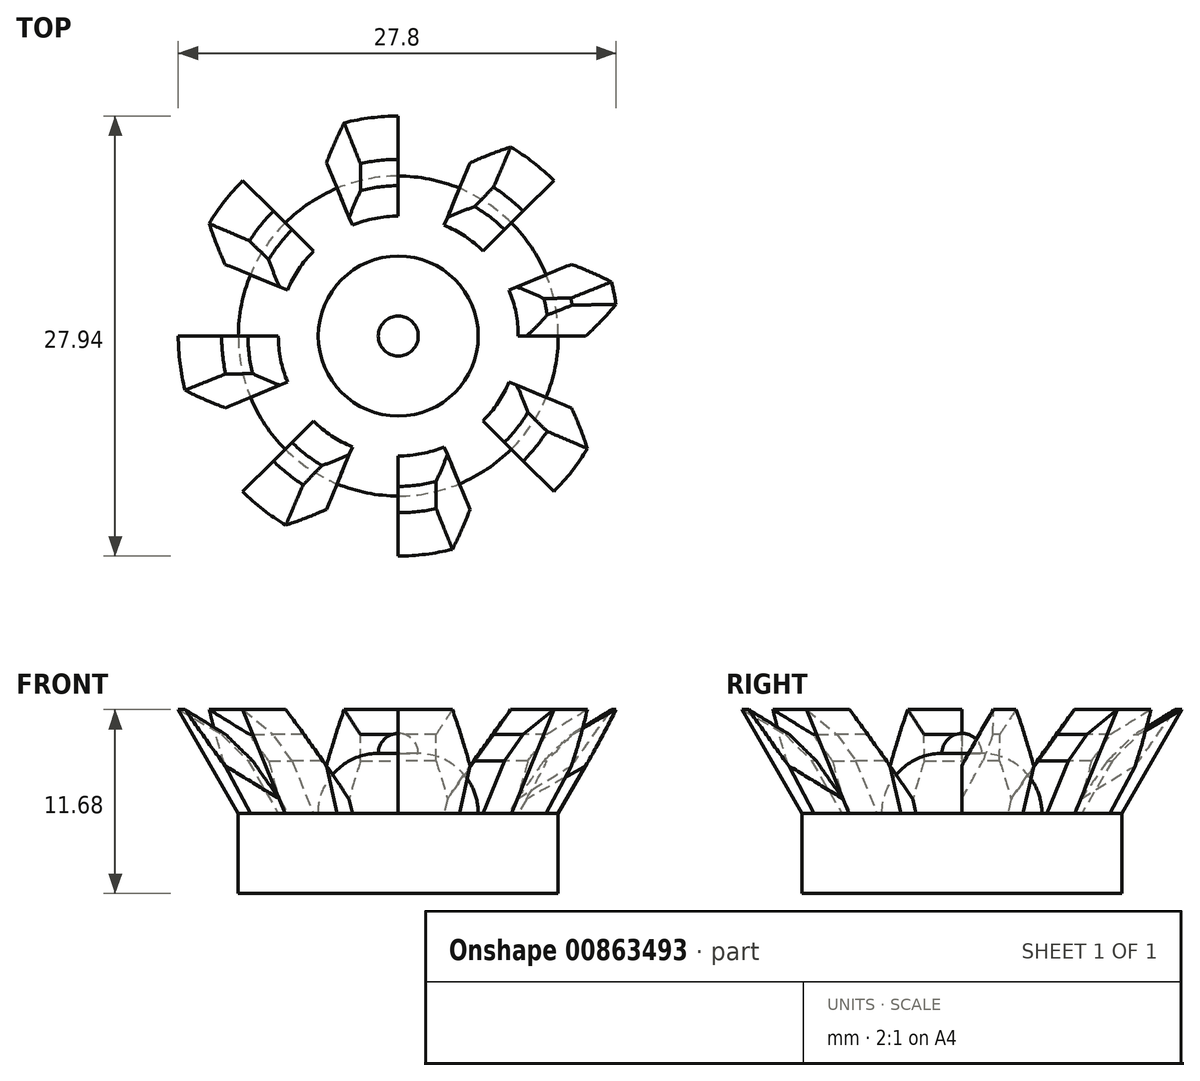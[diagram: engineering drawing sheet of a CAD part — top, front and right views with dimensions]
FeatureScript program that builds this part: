
annotation { "Feature Type Name" : "Feature", "Feature Type Description" : "" }
export const myFeature = defineFeature(function(context is Context, id is Id, definition is map)
    precondition{}
    {
        {
            var Q0;
            Q0=qCreatedBy(makeId("Top.planeOp"),FACE);
            var sketch = newSketch(context, id + "F0", { "sketchPlane" : qUnion([Q0])});
            skCircle(sketch, "E0", {"center": v(0, 0) * mm, "radius": 10.16 * mm});
            skSolve(sketch);
        }
        {
            var Q0;
            Q0=makeQuery(id+"F0.imprint","IMPRINT",FACE,{"disambiguationData":[TD([[makeQuery(id+"F0.imprint","IMPRINT",EDGE,{"derivedFrom":sQuery(id+"F0.wireOp",EDGE,"E0")}),1.0]])]});
            extrude(context, id + "F1", {"entities" : qUnion([Q0]), "depth" : 5.08 * mm, "offsetDistance" : 25.4 * mm});
        }
        {
            var Q0;
            Q0=qCreatedBy(makeId("Front.planeOp"),FACE);
            var sketch = newSketch(context, id + "F2", { "sketchPlane" : qUnion([Q0])});
            skLineSegment(sketch, "E1", {"start": v(0, 0) * mm, "end": v(0, 5.08) * mm, "construction": true});
            skLineSegment(sketch, "E2", {"start": v(0, 5.08) * mm, "end": v(7.62, 5.08) * mm, "construction": true});
            skLineSegment(sketch, "E3", {"start": v(7.62, 5.08) * mm, "end": v(10.16, 5.08) * mm});
            skLineSegment(sketch, "E4", {"start": v(10.16, 5.08) * mm, "end": v(13.97, 11.68) * mm});
            skLineSegment(sketch, "E5", {"start": v(13.97, 11.68) * mm, "end": v(10.16, 9.48) * mm});
            skLineSegment(sketch, "E6", {"start": v(10.16, 9.48) * mm, "end": v(7.62, 5.08) * mm});
            skLineSegment(sketch, "E7.MirrorCS", {"start": v(-10.16, 9.48) * mm, "end": v(-7.62, 5.08) * mm});
            skLineSegment(sketch, "E8.MirrorCS", {"start": v(-13.97, 11.68) * mm, "end": v(-10.16, 9.48) * mm});
            skLineSegment(sketch, "E9.MirrorCS", {"start": v(-10.16, 5.08) * mm, "end": v(-13.97, 11.68) * mm});
            skLineSegment(sketch, "E10.MirrorCS", {"start": v(-7.62, 5.08) * mm, "end": v(-10.16, 5.08) * mm});
            skSolve(sketch);
        }
        {
            var Q0;
            Q0=makeQuery(id+"F2.imprint","IMPRINT",FACE,{"disambiguationData":[TD([[makeQuery(id+"F2.imprint","IMPRINT",EDGE,{"derivedFrom":sQuery(id+"F2.wireOp",EDGE,"E7.MirrorCS")}),-1.0]])]});
            var Q1;
            Q1=makeQuery(id+"F2.imprint","IMPRINT",FACE,{"disambiguationData":[TD([[makeQuery(id+"F2.imprint","IMPRINT",EDGE,{"derivedFrom":sQuery(id+"F2.wireOp",EDGE,"E3")}),1.0]])]});
            var Q2;
            Q2=sQuery(id+"F2.wireOp",EDGE,"E1");
            revolve(context, id + "F3", {"operationType" : NewBodyOperationType.ADD, "surfaceOperationType" : NewSurfaceOperationType.NEW, "entities" : qUnion([Q0, Q1]), "axis" : qUnion([Q2]), "revolveType" : RevolveType.ONE_DIRECTION, "angle" : 157.5 * degree});
        }
        {
            var Q0;
            Q0=makeQuery(id+"F2.imprint","IMPRINT",FACE,{"disambiguationData":[TD([[makeQuery(id+"F2.imprint","IMPRINT",EDGE,{"derivedFrom":sQuery(id+"F2.wireOp",EDGE,"E7.MirrorCS")}),-1.0]])]});
            var Q1;
            Q1=makeQuery(id+"F2.imprint","IMPRINT",FACE,{"disambiguationData":[TD([[makeQuery(id+"F2.imprint","IMPRINT",EDGE,{"derivedFrom":sQuery(id+"F2.wireOp",EDGE,"E3")}),1.0]])]});
            var Q2;
            Q2=sQuery(id+"F2.wireOp",EDGE,"E1");
            revolve(context, id + "F4", {"operationType" : NewBodyOperationType.REMOVE, "surfaceOperationType" : NewSurfaceOperationType.NEW, "entities" : qUnion([Q0, Q1]), "axis" : qUnion([Q2]), "revolveType" : RevolveType.ONE_DIRECTION, "angle" : 135 * degree});
        }
        {
            var Q0;
            Q0=makeQuery(id+"F2.imprint","IMPRINT",FACE,{"disambiguationData":[TD([[makeQuery(id+"F2.imprint","IMPRINT",EDGE,{"derivedFrom":sQuery(id+"F2.wireOp",EDGE,"E7.MirrorCS")}),-1.0]])]});
            var Q1;
            Q1=makeQuery(id+"F2.imprint","IMPRINT",FACE,{"disambiguationData":[TD([[makeQuery(id+"F2.imprint","IMPRINT",EDGE,{"derivedFrom":sQuery(id+"F2.wireOp",EDGE,"E3")}),1.0]])]});
            var Q2;
            Q2=sQuery(id+"F2.wireOp",EDGE,"E1");
            revolve(context, id + "F5", {"operationType" : NewBodyOperationType.ADD, "surfaceOperationType" : NewSurfaceOperationType.NEW, "entities" : qUnion([Q0, Q1]), "axis" : qUnion([Q2]), "revolveType" : RevolveType.ONE_DIRECTION, "angle" : 112.5 * degree});
        }
        {
            var Q0;
            Q0=makeQuery(id+"F2.imprint","IMPRINT",FACE,{"disambiguationData":[TD([[makeQuery(id+"F2.imprint","IMPRINT",EDGE,{"derivedFrom":sQuery(id+"F2.wireOp",EDGE,"E3")}),1.0]])]});
            var Q1;
            Q1=makeQuery(id+"F2.imprint","IMPRINT",FACE,{"disambiguationData":[TD([[makeQuery(id+"F2.imprint","IMPRINT",EDGE,{"derivedFrom":sQuery(id+"F2.wireOp",EDGE,"E7.MirrorCS")}),-1.0]])]});
            var Q2;
            Q2=sQuery(id+"F2.wireOp",EDGE,"E1");
            revolve(context, id + "F6", {"operationType" : NewBodyOperationType.REMOVE, "surfaceOperationType" : NewSurfaceOperationType.NEW, "entities" : qUnion([Q0, Q1]), "axis" : qUnion([Q2]), "revolveType" : RevolveType.ONE_DIRECTION, "angle" : 90 * degree});
        }
        {
            var Q0;
            Q0=makeQuery(id+"F2.imprint","IMPRINT",FACE,{"disambiguationData":[TD([[makeQuery(id+"F2.imprint","IMPRINT",EDGE,{"derivedFrom":sQuery(id+"F2.wireOp",EDGE,"E3")}),1.0]])]});
            var Q1;
            Q1=makeQuery(id+"F2.imprint","IMPRINT",FACE,{"disambiguationData":[TD([[makeQuery(id+"F2.imprint","IMPRINT",EDGE,{"derivedFrom":sQuery(id+"F2.wireOp",EDGE,"E7.MirrorCS")}),-1.0]])]});
            var Q2;
            Q2=sQuery(id+"F2.wireOp",EDGE,"E1");
            revolve(context, id + "F7", {"operationType" : NewBodyOperationType.ADD, "surfaceOperationType" : NewSurfaceOperationType.NEW, "entities" : qUnion([Q0, Q1]), "axis" : qUnion([Q2]), "revolveType" : RevolveType.ONE_DIRECTION, "angle" : 67.5 * degree});
        }
        {
            var Q0;
            Q0=makeQuery(id+"F2.imprint","IMPRINT",FACE,{"disambiguationData":[TD([[makeQuery(id+"F2.imprint","IMPRINT",EDGE,{"derivedFrom":sQuery(id+"F2.wireOp",EDGE,"E3")}),1.0]])]});
            var Q1;
            Q1=makeQuery(id+"F2.imprint","IMPRINT",FACE,{"disambiguationData":[TD([[makeQuery(id+"F2.imprint","IMPRINT",EDGE,{"derivedFrom":sQuery(id+"F2.wireOp",EDGE,"E7.MirrorCS")}),-1.0]])]});
            var Q2;
            Q2=sQuery(id+"F2.wireOp",EDGE,"E1");
            revolve(context, id + "F8", {"operationType" : NewBodyOperationType.REMOVE, "surfaceOperationType" : NewSurfaceOperationType.NEW, "entities" : qUnion([Q0, Q1]), "axis" : qUnion([Q2]), "revolveType" : RevolveType.ONE_DIRECTION, "angle" : 45 * degree});
        }
        {
            var Q0;
            Q0=makeQuery(id+"F2.imprint","IMPRINT",FACE,{"disambiguationData":[TD([[makeQuery(id+"F2.imprint","IMPRINT",EDGE,{"derivedFrom":sQuery(id+"F2.wireOp",EDGE,"E7.MirrorCS")}),-1.0]])]});
            var Q1;
            Q1=makeQuery(id+"F2.imprint","IMPRINT",FACE,{"disambiguationData":[TD([[makeQuery(id+"F2.imprint","IMPRINT",EDGE,{"derivedFrom":sQuery(id+"F2.wireOp",EDGE,"E3")}),1.0]])]});
            var Q2;
            Q2=sQuery(id+"F2.wireOp",EDGE,"E1");
            revolve(context, id + "F9", {"operationType" : NewBodyOperationType.ADD, "surfaceOperationType" : NewSurfaceOperationType.NEW, "entities" : qUnion([Q0, Q1]), "axis" : qUnion([Q2]), "revolveType" : RevolveType.ONE_DIRECTION, "angle" : 22.5 * degree});
        }
        {
            var Q0;
            Q0=makeQuery(id+"F3.opRevolve","CAP_EDGE",EDGE,{"disambiguationData":[OSD([sQuery(id+"F2.wireOp",EDGE,"E5")])],"isStart":false});
            var Q1;
            Q1=makeQuery(id+"F4.boolean.opBoolean","COPY",EDGE,{"derivedFrom":makeQuery(id+"F4.opRevolve","CAP_EDGE",EDGE,{"disambiguationData":[OSD([sQuery(id+"F2.wireOp",EDGE,"E5")])],"isStart":false})});
            var Q2;
            Q2=makeQuery(id+"F5.opRevolve","CAP_EDGE",EDGE,{"disambiguationData":[OSD([sQuery(id+"F2.wireOp",EDGE,"E5")])],"isStart":false});
            var Q3;
            Q3=makeQuery(id+"F6.boolean.opBoolean","COPY",EDGE,{"derivedFrom":makeQuery(id+"F6.opRevolve","CAP_EDGE",EDGE,{"disambiguationData":[OSD([sQuery(id+"F2.wireOp",EDGE,"E5")]),OD(0.0)],"isStart":false})});
            var Q4;
            Q4=makeQuery(id+"F7.opRevolve","CAP_EDGE",EDGE,{"disambiguationData":[OSD([sQuery(id+"F2.wireOp",EDGE,"E5")]),OD(0.0)],"isStart":false});
            var Q5;
            Q5=makeQuery(id+"F8.boolean.opBoolean","COPY",EDGE,{"derivedFrom":makeQuery(id+"F8.opRevolve","CAP_EDGE",EDGE,{"disambiguationData":[OSD([sQuery(id+"F2.wireOp",EDGE,"E5")]),OD(1.0)],"isStart":false})});
            var Q6;
            Q6=makeQuery(id+"F9.opRevolve","CAP_EDGE",EDGE,{"disambiguationData":[OSD([sQuery(id+"F2.wireOp",EDGE,"E5")])],"isStart":false});
            var Q7;
            Q7=makeQuery(id+"F9.opRevolve","CAP_EDGE",EDGE,{"disambiguationData":[OSD([sQuery(id+"F2.wireOp",EDGE,"E5")])],"isStart":true});
            var Q8;
            Q8=makeQuery(id+"F3.opRevolve","CAP_EDGE",EDGE,{"disambiguationData":[OSD([sQuery(id+"F2.wireOp",EDGE,"E8.MirrorCS")]),OD(1.0)],"isStart":false});
            var Q9;
            Q9=makeQuery(id+"F4.boolean.opBoolean","COPY",EDGE,{"derivedFrom":makeQuery(id+"F4.opRevolve","CAP_EDGE",EDGE,{"disambiguationData":[OSD([sQuery(id+"F2.wireOp",EDGE,"E8.MirrorCS")]),OD(1.0)],"isStart":false})});
            var Q10;
            Q10=makeQuery(id+"F5.opRevolve","CAP_EDGE",EDGE,{"disambiguationData":[OSD([sQuery(id+"F2.wireOp",EDGE,"E8.MirrorCS")]),OD(1.0)],"isStart":false});
            var Q11;
            Q11=makeQuery(id+"F6.boolean.opBoolean","COPY",EDGE,{"derivedFrom":makeQuery(id+"F6.opRevolve","CAP_EDGE",EDGE,{"disambiguationData":[OSD([sQuery(id+"F2.wireOp",EDGE,"E8.MirrorCS")])],"isStart":false})});
            var Q12;
            Q12=makeQuery(id+"F7.opRevolve","CAP_EDGE",EDGE,{"disambiguationData":[OSD([sQuery(id+"F2.wireOp",EDGE,"E8.MirrorCS")])],"isStart":false});
            var Q13;
            Q13=makeQuery(id+"F8.boolean.opBoolean","COPY",EDGE,{"derivedFrom":makeQuery(id+"F8.opRevolve","CAP_EDGE",EDGE,{"disambiguationData":[OSD([sQuery(id+"F2.wireOp",EDGE,"E8.MirrorCS")])],"isStart":false})});
            var Q14;
            Q14=makeQuery(id+"F9.opRevolve","CAP_EDGE",EDGE,{"disambiguationData":[OSD([sQuery(id+"F2.wireOp",EDGE,"E8.MirrorCS")]),OD(0.0)],"isStart":false});
            var Q15;
            Q15=makeQuery(id+"F9.opRevolve","CAP_EDGE",EDGE,{"disambiguationData":[OSD([sQuery(id+"F2.wireOp",EDGE,"E8.MirrorCS")]),OD(1.0)],"isStart":false});
            chamfer(context, id + "F10", {"entities" : qUnion([Q0, Q1, Q2, Q3, Q4, Q5, Q6, Q7, Q8, Q9, Q10, Q11, Q12, Q13, Q14, Q15]), "width" : 2.16 * mm, "tangentPropagation" : true});
        }
        {
            var Q0;
            Q0=makeQuery(id+"F3.opRevolve","SWEPT_EDGE",EDGE,{"disambiguationData":[OSD([sQuery(id+"F2.wireOp",EDGE,"E5"),sQuery(id+"F2.wireOp",EDGE,"E6")])]});
            var Q1;
            Q1=makeQuery(id+"F5.opRevolve","SWEPT_EDGE",EDGE,{"disambiguationData":[OSD([sQuery(id+"F2.wireOp",EDGE,"E5"),sQuery(id+"F2.wireOp",EDGE,"E6")])]});
            var Q2;
            Q2=makeQuery(id+"F7.opRevolve","SWEPT_EDGE",EDGE,{"disambiguationData":[OSD([sQuery(id+"F2.wireOp",EDGE,"E5"),sQuery(id+"F2.wireOp",EDGE,"E6")])]});
            var Q3;
            Q3=makeQuery(id+"F9.opRevolve","SWEPT_EDGE",EDGE,{"disambiguationData":[OSD([sQuery(id+"F2.wireOp",EDGE,"E5"),sQuery(id+"F2.wireOp",EDGE,"E6")])]});
            var Q4;
            Q4=makeQuery(id+"F3.opRevolve","SWEPT_EDGE",EDGE,{"disambiguationData":[OSD([sQuery(id+"F2.wireOp",EDGE,"E7.MirrorCS"),sQuery(id+"F2.wireOp",EDGE,"E8.MirrorCS")])]});
            var Q5;
            Q5=makeQuery(id+"F5.opRevolve","SWEPT_EDGE",EDGE,{"disambiguationData":[OSD([sQuery(id+"F2.wireOp",EDGE,"E7.MirrorCS"),sQuery(id+"F2.wireOp",EDGE,"E8.MirrorCS")])]});
            var Q6;
            Q6=makeQuery(id+"F7.opRevolve","SWEPT_EDGE",EDGE,{"disambiguationData":[OSD([sQuery(id+"F2.wireOp",EDGE,"E7.MirrorCS"),sQuery(id+"F2.wireOp",EDGE,"E8.MirrorCS")])]});
            var Q7;
            Q7=makeQuery(id+"F9.opRevolve","SWEPT_EDGE",EDGE,{"disambiguationData":[OSD([sQuery(id+"F2.wireOp",EDGE,"E7.MirrorCS"),sQuery(id+"F2.wireOp",EDGE,"E8.MirrorCS")])]});
            chamfer(context, id + "F11", {"entities" : qUnion([Q0, Q1, Q2, Q3, Q4, Q5, Q6, Q7]), "width" : 4.57 * mm, "tangentPropagation" : true});
        }
        {
            var Q0;
            {var subQ0=sQuery(id+"F2.wireOp",EDGE,"E10.MirrorCS");var subQ1=sQuery(id+"F2.wireOp",EDGE,"E3");Q0=makeQuery(id+"F8.boolean.opBoolean","MERGE",FACE,{"derivedFrom":[makeQuery(id+"F6.boolean.opBoolean","MERGE",FACE,{"derivedFrom":[makeQuery(id+"F4.boolean.opBoolean","MERGE",FACE,{"derivedFrom":[makeQuery(id+"F1.opExtrude","CAP_FACE",FACE,{"disambiguationData":[OSD([sQuery(id+"F0.wireOp",EDGE,"E0")])],"isStart":false}),makeQuery(id+"F4.opRevolve","SWEPT_FACE",FACE,{"disambiguationData":[OSD([subQ1])]}),makeQuery(id+"F4.opRevolve","SWEPT_FACE",FACE,{"disambiguationData":[OSD([subQ0])]})]}),makeQuery(id+"F6.opRevolve","SWEPT_FACE",FACE,{"disambiguationData":[OSD([subQ1])]}),makeQuery(id+"F6.opRevolve","SWEPT_FACE",FACE,{"disambiguationData":[OSD([subQ0])]})]}),makeQuery(id+"F8.opRevolve","SWEPT_FACE",FACE,{"disambiguationData":[OSD([subQ1])]}),makeQuery(id+"F8.opRevolve","SWEPT_FACE",FACE,{"disambiguationData":[OSD([subQ0])]})]});}
            var sketch = newSketch(context, id + "F12", { "sketchPlane" : qUnion([Q0])});
            skCircle(sketch, "E11", {"center": v(0, 0) * mm, "radius": 5.08 * mm});
            skSolve(sketch);
        }
        {
            var Q0;
            Q0=makeQuery(id+"F12.imprint","IMPRINT",FACE,{"disambiguationData":[TD([[makeQuery(id+"F12.imprint","IMPRINT",EDGE,{"derivedFrom":sQuery(id+"F12.wireOp",EDGE,"E11")}),1.0]])]});
            extrude(context, id + "F13", {"entities" : qUnion([Q0]), "operationType" : NewBodyOperationType.ADD, "depth" : 3.8 * mm, "offsetDistance" : 25.4 * mm});
        }
        {
            var Q0;
            Q0=makeQuery(id+"F13.opExtrude","CAP_EDGE",EDGE,{"disambiguationData":[OSD([sQuery(id+"F12.wireOp",EDGE,"E11")])],"isStart":false});
            fillet(context, id + "F14", {"entities" : qUnion([Q0]), "radius" : 3.8 * mm, "tangentPropagation" : true, "allowEdgeOverflow" : false});
        }
        {
            var Q0;
            Q0=makeQuery(id+"F13.opExtrude","CAP_FACE",FACE,{"disambiguationData":[OSD([sQuery(id+"F12.wireOp",EDGE,"E11")])],"isStart":false});
            extrude(context, id + "F15", {"entities" : qUnion([Q0]), "operationType" : NewBodyOperationType.ADD, "depth" : 1.27 * mm, "offsetDistance" : 25.4 * mm});
        }
        {
            var Q0;
            Q0=makeQuery(id+"F15.opExtrude","CAP_FACE",FACE,{"disambiguationData":[OSD([sQuery(id+"F12.wireOp",EDGE,"E11")])],"isStart":false});
            fillet(context, id + "F16", {"entities" : qUnion([Q0]), "radius" : 1.27 * mm, "tangentPropagation" : true, "allowEdgeOverflow" : false});
        }
    });
